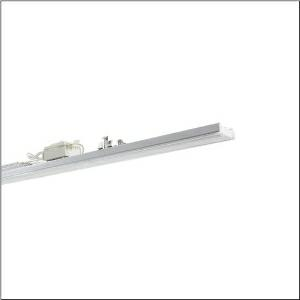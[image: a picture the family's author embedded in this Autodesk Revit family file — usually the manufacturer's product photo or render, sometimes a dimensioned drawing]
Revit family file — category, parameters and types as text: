
# Revit family: licross_r__21_recessed_mo_52tl19cn485g_b288
name_source: partatom
category: Lighting Fixtures
units: mm (PartAtom-declared; Revit-internal decimal feet)

## family parameters
Cut with Voids When Loaded = No
Host = Face
Light Source = No
Part Type = Normal
Room Calculation Point = No
Round Connector Dimension = Use Diameter
Shared = No

## types (1)
- --- (1 x LED, 8870 lm, 49.9 W, 4000K)
    Apparent Load = 50 VA
    CIE Flux Codes = 55 90 98 100 100
    Color Rendering = 80
    Color Temperature = 4000K
    Default Elevation = 1800 mm
    Description = Licross® 21 Recessed MO, luminaire insert, of sheet steel, galvanised, coil coated, white, length: 1.500mm, width: 66mm, height: 67mm, LED rated luminous flux: 8.880lm, light colour: 840, control gear: ON/OFF Multilumen, CLOi, control gear: ECG DALI, with plug, 5-pole, with phase selection, mains connection: 220..240V, AC, 50/60Hz, start of lifetime: 50W, end of service life: 61W, internal wiring halogen-free, primary light control with lens, of plastic, primary optical cover: cover, of PMMA, light emission: direct distribution, primary light characteristic: double asymmetric, protection rating (complete): IP40, insulation class (complete): insulation class I (protective earthing), certification: CE, ENEC, VDE, UKCA, protection symbol: D if used in an environment without relevant dust loads with corresponding accessories, impact resistance: IK06, permissible ambient temperature for indoor applications: -35..+40°C, corresponds to IFS (International Featured Standards) requirements for safety and quality in the food industry, reducing of maximum allowable ambient temperature of 5°C with ceiling mounting, LABS conformity tested according to VDMA 24364:2018-05, packaging unit: 1 piece
    Height = 58 mm
    Lamp = 1 x LED
    Lamp Light Flux = 8870 lm
    Lamp Power = 49.9 W
    Lamp count = 1
    Length = 1500 mm
    Luminous efficacy = 178 lm/W
    Manufacturer = Siteco
    ModVariant = No
    Model = 52TL19CN485G
    Mounting Place = Ceiling
    Mounting Type = Pendant
    Number of Poles = 1
    OnlyDefault = Yes
    Power Factor = 1
    Product Name = Licross® 21 Recessed MO
    Product group = luminaire insert | ceiling pendant
    ProductGroupID = 902
    Protection Class = Protection class I
    Protection Degree = IP 40
    RLX_Detail_Level = 1
    RLX_Emergency_Light_Flux = 0 lm
    RLX_Emergency_Type = 0
    RLX_Emergency_Type_DB = No
    RlxData = <blob elided: 22357 chars, md5=c6e02179>
    Socket = socket
    Standby Power = 0 W
    System Light Flux = 8870 lm
    System Power = 50 W
    Type Comments = factory setting: luminous flux: 100 % | (A | C | E) | 116 mA
    Type Image = l_1296930.jpg
    URL = http://relux.com
    VarID = @adj_132291
    Voltage = 0 V
    Weight = 0.00 kg
    Width = 66 mm

## geometry (parser evidence)
native form markers: Blend x4, Sweep x10
no freeform markers — native parametric forms only
